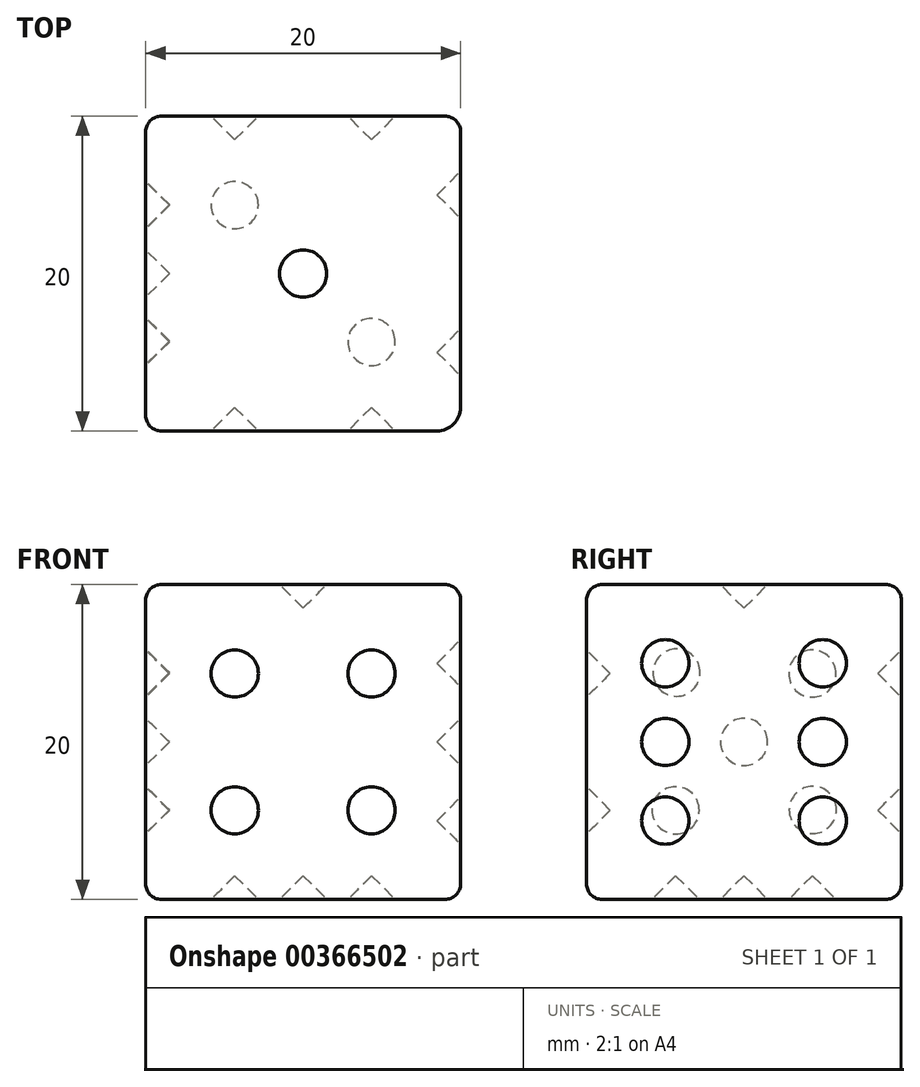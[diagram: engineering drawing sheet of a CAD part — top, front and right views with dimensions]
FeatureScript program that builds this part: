
annotation { "Feature Type Name" : "Feature", "Feature Type Description" : "" }
export const myFeature = defineFeature(function(context is Context, id is Id, definition is map)
    precondition{}
    {
        {
            var Q0;
            Q0=qCreatedBy(makeId("Top.planeOp"),FACE);
            var sketch = newSketch(context, id + "F0", { "sketchPlane" : qUnion([Q0])});
            skLineSegment(sketch, "E0.bottom", {"start": v(0, 0) * mm, "end": v(20, 0) * mm});
            skLineSegment(sketch, "E0.top", {"start": v(0, 20) * mm, "end": v(20, 20) * mm});
            skLineSegment(sketch, "E0.left", {"start": v(0, 0) * mm, "end": v(0, 20) * mm});
            skLineSegment(sketch, "E1", {"start": v(20, 20) * mm, "end": v(20, 0) * mm});
            skSolve(sketch);
        }
        {
            var Q0;
            Q0=qSketchRegion(id+"F0",true);
            extrude(context, id + "F1", {"entities" : qUnion([Q0]), "depth" : 20 * mm});
        }
        {
            var Q0;
            Q0=makeQuery(id+"F1.opExtrude","CAP_FACE",FACE,{"disambiguationData":[OSD([sQuery(id+"F0.wireOp",EDGE,"E0.bottom"),sQuery(id+"F0.wireOp",EDGE,"E0.top"),sQuery(id+"F0.wireOp",EDGE,"E0.left"),sQuery(id+"F0.wireOp",EDGE,"E1")])],"isStart":false});
            var sketch = newSketch(context, id + "F2", { "sketchPlane" : qUnion([Q0])});
            skLineSegment(sketch, "E2", {"start": v(10, 20) * mm, "end": v(10, 0) * mm, "construction": true});
            skCircle(sketch, "E3", {"center": v(10, 10) * mm, "radius": 1.5 * mm});
            skSolve(sketch);
        }
        {
            var Q0;
            Q0=makeQuery(id+"F2.imprint","IMPRINT",FACE,{"disambiguationData":[TD([[makeQuery(id+"F2.imprint","IMPRINT",EDGE,{"derivedFrom":sQuery(id+"F2.wireOp",EDGE,"E3")}),1.0]])]});
            var Q1;
            Q1=sQuery(id+"F2.wireOp",EDGE,"E3");
            extrude(context, id + "F3", {"entities" : qUnion([Q0]), "operationType" : NewBodyOperationType.REMOVE, "surfaceEntities" : qUnion([Q1]), "oppositeDirection" : true, "depth" : 1.5 * mm});
        }
        {
            var Q0;
            Q0=makeQuery(id+"F1.opExtrude","SWEPT_FACE",FACE,{"disambiguationData":[OSD([sQuery(id+"F0.wireOp",EDGE,"E0.top")])]});
            var sketch = newSketch(context, id + "F4", { "sketchPlane" : qUnion([Q0])});
            skLineSegment(sketch, "E4", {"start": v(-20, 20) * mm, "end": v(-14.34, 14.34) * mm, "construction": true});
            skLineSegment(sketch, "E5", {"start": v(0, 0) * mm, "end": v(-5.66, 5.66) * mm, "construction": true});
            skCircle(sketch, "E6", {"center": v(-14.34, 14.34) * mm, "radius": 1.5 * mm});
            skCircle(sketch, "E7", {"center": v(-5.66, 5.66) * mm, "radius": 1.5 * mm});
            skSolve(sketch);
        }
        {
            var Q0;
            Q0=qSketchRegion(id+"F4",true);
            extrude(context, id + "F5", {"entities" : qUnion([Q0]), "operationType" : NewBodyOperationType.REMOVE, "oppositeDirection" : true, "depth" : 1.5 * mm});
        }
        {
            var Q0;
            Q0=makeQuery(id+"F1.opExtrude","SWEPT_EDGE",EDGE,{"disambiguationData":[OSD([sQuery(id+"F0.wireOp",EDGE,"E0.bottom"),sQuery(id+"F0.wireOp",EDGE,"E0.left")])]});
            var Q1;
            Q1=makeQuery(id+"F1.opExtrude","CAP_EDGE",EDGE,{"disambiguationData":[OSD([sQuery(id+"F0.wireOp",EDGE,"E0.left")])],"isStart":true});
            var Q2;
            Q2=makeQuery(id+"F1.opExtrude","SWEPT_EDGE",EDGE,{"disambiguationData":[OSD([sQuery(id+"F0.wireOp",EDGE,"E0.top"),sQuery(id+"F0.wireOp",EDGE,"E1")])]});
            var Q3;
            Q3=makeQuery(id+"F1.opExtrude","SWEPT_EDGE",EDGE,{"disambiguationData":[OSD([sQuery(id+"F0.wireOp",EDGE,"E0.top"),sQuery(id+"F0.wireOp",EDGE,"E0.left")])]});
            var Q4;
            Q4=makeQuery(id+"F1.opExtrude","CAP_EDGE",EDGE,{"disambiguationData":[OSD([sQuery(id+"F0.wireOp",EDGE,"E0.top")])],"isStart":false});
            var Q5;
            Q5=makeQuery(id+"F1.opExtrude","CAP_EDGE",EDGE,{"disambiguationData":[OSD([sQuery(id+"F0.wireOp",EDGE,"E0.left")])],"isStart":false});
            var Q6;
            Q6=makeQuery(id+"F1.opExtrude","CAP_EDGE",EDGE,{"disambiguationData":[OSD([sQuery(id+"F0.wireOp",EDGE,"E0.bottom")])],"isStart":true});
            var Q7;
            Q7=makeQuery(id+"F1.opExtrude","CAP_EDGE",EDGE,{"disambiguationData":[OSD([sQuery(id+"F0.wireOp",EDGE,"E1")])],"isStart":true});
            var Q8;
            Q8=makeQuery(id+"F1.opExtrude","CAP_EDGE",EDGE,{"disambiguationData":[OSD([sQuery(id+"F0.wireOp",EDGE,"E1")])],"isStart":false});
            var Q9;
            Q9=makeQuery(id+"F1.opExtrude","CAP_EDGE",EDGE,{"disambiguationData":[OSD([sQuery(id+"F0.wireOp",EDGE,"E0.bottom")])],"isStart":false});
            var Q10;
            Q10=makeQuery(id+"F1.opExtrude","CAP_EDGE",EDGE,{"disambiguationData":[OSD([sQuery(id+"F0.wireOp",EDGE,"E0.top")])],"isStart":true});
            fillet(context, id + "F6", {"entities" : qUnion([Q0, Q1, Q2, Q3, Q4, Q5, Q6, Q7, Q8, Q9, Q10]), "radius" : 1 * mm, "tangentPropagation" : true, "allowEdgeOverflow" : false});
        }
        {
            var Q0;
            Q0=makeQuery(id+"F5.boolean.opBoolean","COPY",EDGE,{"derivedFrom":makeQuery(id+"F5.opExtrude","CAP_EDGE",EDGE,{"disambiguationData":[OSD([sQuery(id+"F4.wireOp",EDGE,"E7")])],"isStart":false})});
            chamfer(context, id + "F7", {"entities" : qUnion([Q0]), "width" : 1.5 * mm, "tangentPropagation" : true});
        }
        {
            var Q0;
            Q0=makeQuery(id+"F1.opExtrude","CAP_FACE",FACE,{"disambiguationData":[OSD([sQuery(id+"F0.wireOp",EDGE,"E0.bottom"),sQuery(id+"F0.wireOp",EDGE,"E0.top"),sQuery(id+"F0.wireOp",EDGE,"E0.left"),sQuery(id+"F0.wireOp",EDGE,"E1")])],"isStart":true});
            var sketch = newSketch(context, id + "F8", { "sketchPlane" : qUnion([Q0])});
            skCircle(sketch, "E8", {"center": v(5.66, -14.34) * mm, "radius": 1.5 * mm});
            skCircle(sketch, "E9", {"center": v(14.34, -5.66) * mm, "radius": 1.5 * mm});
            skCircle(sketch, "E10", {"center": v(10, -10) * mm, "radius": 1.5 * mm});
            skSolve(sketch);
        }
        {
            var Q0;
            Q0=makeQuery(id+"F8.imprint","IMPRINT",FACE,{"disambiguationData":[TD([[makeQuery(id+"F8.imprint","IMPRINT",EDGE,{"derivedFrom":sQuery(id+"F8.wireOp",EDGE,"E8")}),1.0]])]});
            var Q1;
            Q1=makeQuery(id+"F8.imprint","IMPRINT",FACE,{"disambiguationData":[TD([[makeQuery(id+"F8.imprint","IMPRINT",EDGE,{"derivedFrom":sQuery(id+"F8.wireOp",EDGE,"E10")}),1.0]])]});
            var Q2;
            Q2=makeQuery(id+"F8.imprint","IMPRINT",FACE,{"disambiguationData":[TD([[makeQuery(id+"F8.imprint","IMPRINT",EDGE,{"derivedFrom":sQuery(id+"F8.wireOp",EDGE,"E9")}),1.0]])]});
            extrude(context, id + "F9", {"entities" : qUnion([Q0, Q1, Q2]), "operationType" : NewBodyOperationType.REMOVE, "oppositeDirection" : true, "depth" : 1.5 * mm});
        }
        {
            var Q0;
            Q0=makeQuery(id+"F5.boolean.opBoolean","COPY",FACE,{"derivedFrom":makeQuery(id+"F5.opExtrude","CAP_FACE",FACE,{"disambiguationData":[OSD([sQuery(id+"F4.wireOp",EDGE,"E6")])],"isStart":false})});
            chamfer(context, id + "F10", {"entities" : qUnion([Q0]), "width" : 1.5 * mm, "tangentPropagation" : true});
        }
        {
            var Q0;
            Q0=makeQuery(id+"F3.boolean.opBoolean","COPY",EDGE,{"derivedFrom":makeQuery(id+"F3.opExtrude","CAP_EDGE",EDGE,{"disambiguationData":[OSD([sQuery(id+"F2.wireOp",EDGE,"E3")])],"isStart":false})});
            chamfer(context, id + "F11", {"entities" : qUnion([Q0]), "width" : 1.5 * mm, "tangentPropagation" : true});
        }
        {
            var Q0;
            Q0=makeQuery(id+"F1.opExtrude","SWEPT_EDGE",EDGE,{"disambiguationData":[OSD([sQuery(id+"F0.wireOp",EDGE,"E0.bottom"),sQuery(id+"F0.wireOp",EDGE,"E1")])]});
            fillet(context, id + "F12", {"entities" : qUnion([Q0]), "radius" : 1.5 * mm, "tangentPropagation" : true, "allowEdgeOverflow" : false});
        }
        {
            var Q0;
            Q0=makeQuery(id+"F9.boolean.opBoolean","COPY",EDGE,{"derivedFrom":makeQuery(id+"F9.opExtrude","CAP_EDGE",EDGE,{"disambiguationData":[OSD([sQuery(id+"F8.wireOp",EDGE,"E8")])],"isStart":false})});
            var Q1;
            Q1=makeQuery(id+"F9.boolean.opBoolean","COPY",EDGE,{"derivedFrom":makeQuery(id+"F9.opExtrude","CAP_EDGE",EDGE,{"disambiguationData":[OSD([sQuery(id+"F8.wireOp",EDGE,"E10")])],"isStart":false})});
            var Q2;
            Q2=makeQuery(id+"F9.boolean.opBoolean","COPY",EDGE,{"derivedFrom":makeQuery(id+"F9.opExtrude","CAP_EDGE",EDGE,{"disambiguationData":[OSD([sQuery(id+"F8.wireOp",EDGE,"E9")])],"isStart":false})});
            chamfer(context, id + "F13", {"entities" : qUnion([Q0, Q1, Q2]), "width" : 1.5 * mm, "tangentPropagation" : true});
        }
        {
            var Q0;
            Q0=makeQuery(id+"F1.opExtrude","SWEPT_FACE",FACE,{"disambiguationData":[OSD([sQuery(id+"F0.wireOp",EDGE,"E0.bottom")])]});
            var sketch = newSketch(context, id + "F14", { "sketchPlane" : qUnion([Q0])});
            skCircle(sketch, "E11", {"center": v(5.66, 14.34) * mm, "radius": 1.5 * mm});
            skCircle(sketch, "E12", {"center": v(14.34, 5.66) * mm, "radius": 1.5 * mm});
            skCircle(sketch, "E13", {"center": v(5.66, 5.66) * mm, "radius": 1.5 * mm});
            skCircle(sketch, "E14", {"center": v(14.34, 14.34) * mm, "radius": 1.5 * mm});
            skSolve(sketch);
        }
        {
            var Q0;
            Q0=makeQuery(id+"F14.imprint","IMPRINT",FACE,{"disambiguationData":[TD([[makeQuery(id+"F14.imprint","IMPRINT",EDGE,{"derivedFrom":sQuery(id+"F14.wireOp",EDGE,"E13")}),1.0]])]});
            var Q1;
            Q1=makeQuery(id+"F14.imprint","IMPRINT",FACE,{"disambiguationData":[TD([[makeQuery(id+"F14.imprint","IMPRINT",EDGE,{"derivedFrom":sQuery(id+"F14.wireOp",EDGE,"E11")}),1.0]])]});
            var Q2;
            Q2=makeQuery(id+"F14.imprint","IMPRINT",FACE,{"disambiguationData":[TD([[makeQuery(id+"F14.imprint","IMPRINT",EDGE,{"derivedFrom":sQuery(id+"F14.wireOp",EDGE,"E14")}),1.0]])]});
            var Q3;
            Q3=makeQuery(id+"F14.imprint","IMPRINT",FACE,{"disambiguationData":[TD([[makeQuery(id+"F14.imprint","IMPRINT",EDGE,{"derivedFrom":sQuery(id+"F14.wireOp",EDGE,"E12")}),1.0]])]});
            extrude(context, id + "F15", {"entities" : qUnion([Q0, Q1, Q2, Q3]), "operationType" : NewBodyOperationType.REMOVE, "oppositeDirection" : true, "depth" : 1.5 * mm});
        }
        {
            var Q0;
            Q0=makeQuery(id+"F15.boolean.opBoolean","COPY",EDGE,{"derivedFrom":makeQuery(id+"F15.opExtrude","CAP_EDGE",EDGE,{"disambiguationData":[OSD([sQuery(id+"F14.wireOp",EDGE,"E11")])],"isStart":false})});
            var Q1;
            Q1=makeQuery(id+"F15.boolean.opBoolean","COPY",EDGE,{"derivedFrom":makeQuery(id+"F15.opExtrude","CAP_EDGE",EDGE,{"disambiguationData":[OSD([sQuery(id+"F14.wireOp",EDGE,"E14")])],"isStart":false})});
            var Q2;
            Q2=makeQuery(id+"F15.boolean.opBoolean","COPY",EDGE,{"derivedFrom":makeQuery(id+"F15.opExtrude","CAP_EDGE",EDGE,{"disambiguationData":[OSD([sQuery(id+"F14.wireOp",EDGE,"E13")])],"isStart":false})});
            var Q3;
            Q3=makeQuery(id+"F15.boolean.opBoolean","COPY",EDGE,{"derivedFrom":makeQuery(id+"F15.opExtrude","CAP_EDGE",EDGE,{"disambiguationData":[OSD([sQuery(id+"F14.wireOp",EDGE,"E12")])],"isStart":false})});
            chamfer(context, id + "F16", {"entities" : qUnion([Q0, Q1, Q2, Q3]), "width" : 1.5 * mm, "tangentPropagation" : true});
        }
        {
            var Q0;
            Q0=makeQuery(id+"F1.opExtrude","SWEPT_FACE",FACE,{"disambiguationData":[OSD([sQuery(id+"F0.wireOp",EDGE,"E0.left")])]});
            var sketch = newSketch(context, id + "F17", { "sketchPlane" : qUnion([Q0])});
            skCircle(sketch, "E15", {"center": v(-14.34, 14.34) * mm, "radius": 1.5 * mm});
            skCircle(sketch, "E16", {"center": v(-14.37, 5.68) * mm, "radius": 1.5 * mm});
            skCircle(sketch, "E17", {"center": v(-5.71, 14.4) * mm, "radius": 1.5 * mm});
            skCircle(sketch, "E18", {"center": v(-5.66, 5.66) * mm, "radius": 1.5 * mm});
            skCircle(sketch, "E19", {"center": v(-10, 10) * mm, "radius": 1.5 * mm});
            skSolve(sketch);
        }
        {
            var Q0;
            Q0=makeQuery(id+"F17.imprint","IMPRINT",FACE,{"disambiguationData":[TD([[makeQuery(id+"F17.imprint","IMPRINT",EDGE,{"derivedFrom":sQuery(id+"F17.wireOp",EDGE,"E15")}),1.0]])]});
            var Q1;
            Q1=makeQuery(id+"F17.imprint","IMPRINT",FACE,{"disambiguationData":[TD([[makeQuery(id+"F17.imprint","IMPRINT",EDGE,{"derivedFrom":sQuery(id+"F17.wireOp",EDGE,"E17")}),1.0]])]});
            var Q2;
            Q2=makeQuery(id+"F17.imprint","IMPRINT",FACE,{"disambiguationData":[TD([[makeQuery(id+"F17.imprint","IMPRINT",EDGE,{"derivedFrom":sQuery(id+"F17.wireOp",EDGE,"E19")}),1.0]])]});
            var Q3;
            Q3=makeQuery(id+"F17.imprint","IMPRINT",FACE,{"disambiguationData":[TD([[makeQuery(id+"F17.imprint","IMPRINT",EDGE,{"derivedFrom":sQuery(id+"F17.wireOp",EDGE,"E16")}),1.0]])]});
            var Q4;
            Q4=makeQuery(id+"F17.imprint","IMPRINT",FACE,{"disambiguationData":[TD([[makeQuery(id+"F17.imprint","IMPRINT",EDGE,{"derivedFrom":sQuery(id+"F17.wireOp",EDGE,"E18")}),1.0]])]});
            extrude(context, id + "F18", {"entities" : qUnion([Q0, Q1, Q2, Q3, Q4]), "operationType" : NewBodyOperationType.REMOVE, "oppositeDirection" : true, "depth" : 1.5 * mm});
        }
        {
            var Q0;
            Q0=makeQuery(id+"F18.boolean.opBoolean","COPY",EDGE,{"derivedFrom":makeQuery(id+"F18.opExtrude","CAP_EDGE",EDGE,{"disambiguationData":[OSD([sQuery(id+"F17.wireOp",EDGE,"E15")])],"isStart":false})});
            var Q1;
            Q1=makeQuery(id+"F18.boolean.opBoolean","COPY",EDGE,{"derivedFrom":makeQuery(id+"F18.opExtrude","CAP_EDGE",EDGE,{"disambiguationData":[OSD([sQuery(id+"F17.wireOp",EDGE,"E16")])],"isStart":false})});
            var Q2;
            Q2=makeQuery(id+"F18.boolean.opBoolean","COPY",EDGE,{"derivedFrom":makeQuery(id+"F18.opExtrude","CAP_EDGE",EDGE,{"disambiguationData":[OSD([sQuery(id+"F17.wireOp",EDGE,"E19")])],"isStart":false})});
            var Q3;
            Q3=makeQuery(id+"F18.boolean.opBoolean","COPY",EDGE,{"derivedFrom":makeQuery(id+"F18.opExtrude","CAP_EDGE",EDGE,{"disambiguationData":[OSD([sQuery(id+"F17.wireOp",EDGE,"E17")])],"isStart":false})});
            var Q4;
            Q4=makeQuery(id+"F18.boolean.opBoolean","COPY",EDGE,{"derivedFrom":makeQuery(id+"F18.opExtrude","CAP_EDGE",EDGE,{"disambiguationData":[OSD([sQuery(id+"F17.wireOp",EDGE,"E18")])],"isStart":false})});
            chamfer(context, id + "F19", {"entities" : qUnion([Q0, Q1, Q2, Q3, Q4]), "width" : 1.5 * mm, "tangentPropagation" : true});
        }
        {
            var Q0;
            Q0=makeQuery(id+"F1.opExtrude","SWEPT_FACE",FACE,{"disambiguationData":[OSD([sQuery(id+"F0.wireOp",EDGE,"E1")])]});
            var sketch = newSketch(context, id + "F20", { "sketchPlane" : qUnion([Q0])});
            skCircle(sketch, "E20", {"center": v(5, 15) * mm, "radius": 1.5 * mm});
            skCircle(sketch, "E21", {"center": v(15, 15) * mm, "radius": 1.5 * mm});
            skCircle(sketch, "E22", {"center": v(5, 10) * mm, "radius": 1.5 * mm});
            skCircle(sketch, "E23", {"center": v(15, 10) * mm, "radius": 1.5 * mm});
            skCircle(sketch, "E24", {"center": v(5, 5) * mm, "radius": 1.5 * mm});
            skCircle(sketch, "E25", {"center": v(15, 5) * mm, "radius": 1.5 * mm});
            skSolve(sketch);
        }
        {
            var Q0;
            Q0=makeQuery(id+"F20.imprint","IMPRINT",FACE,{"disambiguationData":[TD([[makeQuery(id+"F20.imprint","IMPRINT",EDGE,{"derivedFrom":sQuery(id+"F20.wireOp",EDGE,"E21")}),1.0]])]});
            var Q1;
            Q1=makeQuery(id+"F20.imprint","IMPRINT",FACE,{"disambiguationData":[TD([[makeQuery(id+"F20.imprint","IMPRINT",EDGE,{"derivedFrom":sQuery(id+"F20.wireOp",EDGE,"E20")}),1.0]])]});
            var Q2;
            Q2=makeQuery(id+"F20.imprint","IMPRINT",FACE,{"disambiguationData":[TD([[makeQuery(id+"F20.imprint","IMPRINT",EDGE,{"derivedFrom":sQuery(id+"F20.wireOp",EDGE,"E22")}),1.0]])]});
            var Q3;
            Q3=makeQuery(id+"F20.imprint","IMPRINT",FACE,{"disambiguationData":[TD([[makeQuery(id+"F20.imprint","IMPRINT",EDGE,{"derivedFrom":sQuery(id+"F20.wireOp",EDGE,"E23")}),1.0]])]});
            var Q4;
            Q4=makeQuery(id+"F20.imprint","IMPRINT",FACE,{"disambiguationData":[TD([[makeQuery(id+"F20.imprint","IMPRINT",EDGE,{"derivedFrom":sQuery(id+"F20.wireOp",EDGE,"E25")}),1.0]])]});
            var Q5;
            Q5=makeQuery(id+"F20.imprint","IMPRINT",FACE,{"disambiguationData":[TD([[makeQuery(id+"F20.imprint","IMPRINT",EDGE,{"derivedFrom":sQuery(id+"F20.wireOp",EDGE,"E24")}),1.0]])]});
            extrude(context, id + "F21", {"entities" : qUnion([Q0, Q1, Q2, Q3, Q4, Q5]), "operationType" : NewBodyOperationType.REMOVE, "oppositeDirection" : true, "depth" : 1.5 * mm});
        }
        {
            var Q0;
            Q0=makeQuery(id+"F21.boolean.opBoolean","COPY",EDGE,{"derivedFrom":makeQuery(id+"F21.opExtrude","CAP_EDGE",EDGE,{"disambiguationData":[OSD([sQuery(id+"F20.wireOp",EDGE,"E25")])],"isStart":false})});
            var Q1;
            Q1=makeQuery(id+"F21.boolean.opBoolean","COPY",EDGE,{"derivedFrom":makeQuery(id+"F21.opExtrude","CAP_EDGE",EDGE,{"disambiguationData":[OSD([sQuery(id+"F20.wireOp",EDGE,"E23")])],"isStart":false})});
            var Q2;
            Q2=makeQuery(id+"F21.boolean.opBoolean","COPY",EDGE,{"derivedFrom":makeQuery(id+"F21.opExtrude","CAP_EDGE",EDGE,{"disambiguationData":[OSD([sQuery(id+"F20.wireOp",EDGE,"E22")])],"isStart":false})});
            var Q3;
            Q3=makeQuery(id+"F21.boolean.opBoolean","COPY",EDGE,{"derivedFrom":makeQuery(id+"F21.opExtrude","CAP_EDGE",EDGE,{"disambiguationData":[OSD([sQuery(id+"F20.wireOp",EDGE,"E24")])],"isStart":false})});
            var Q4;
            Q4=makeQuery(id+"F21.boolean.opBoolean","COPY",EDGE,{"derivedFrom":makeQuery(id+"F21.opExtrude","CAP_EDGE",EDGE,{"disambiguationData":[OSD([sQuery(id+"F20.wireOp",EDGE,"E20")])],"isStart":false})});
            var Q5;
            Q5=makeQuery(id+"F21.boolean.opBoolean","COPY",EDGE,{"derivedFrom":makeQuery(id+"F21.opExtrude","CAP_EDGE",EDGE,{"disambiguationData":[OSD([sQuery(id+"F20.wireOp",EDGE,"E21")])],"isStart":false})});
            chamfer(context, id + "F22", {"entities" : qUnion([Q0, Q1, Q2, Q3, Q4, Q5]), "width" : 1.5 * mm, "tangentPropagation" : true});
        }
    });
